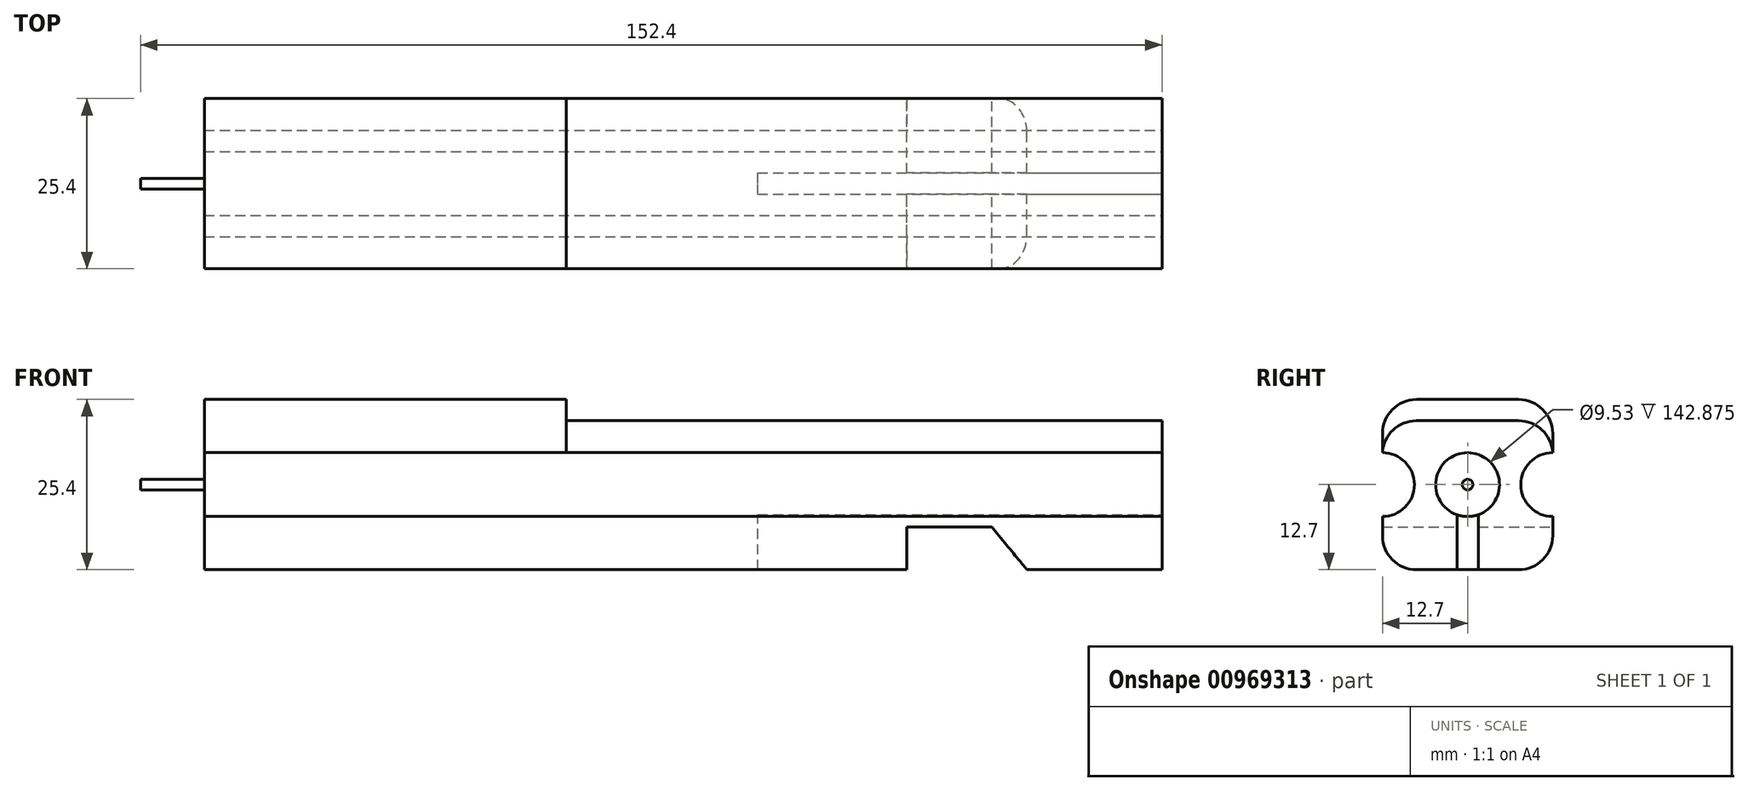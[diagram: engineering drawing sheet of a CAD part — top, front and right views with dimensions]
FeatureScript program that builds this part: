
annotation { "Feature Type Name" : "Feature", "Feature Type Description" : "" }
export const myFeature = defineFeature(function(context is Context, id is Id, definition is map)
    precondition{}
    {
        {
            var Q0;
            Q0=qCreatedBy(makeId("Front.planeOp"),FACE);
            var sketch = newSketch(context, id + "F0", { "sketchPlane" : qUnion([Q0])});
            skLineSegment(sketch, "E0.right", {"start": v(-83.92, 25.4) * mm, "end": v(-83.92, 0) * mm});
            skLineSegment(sketch, "E1.bottom", {"start": v(68.48, 7.94) * mm, "end": v(-74.4, 7.94) * mm});
            skLineSegment(sketch, "E1.top", {"start": v(68.48, 17.46) * mm, "end": v(-74.4, 17.46) * mm});
            skLineSegment(sketch, "E1.left", {"start": v(68.48, 7.94) * mm, "end": v(68.48, 17.46) * mm});
            skLineSegment(sketch, "E1.right", {"start": v(-74.4, 7.94) * mm, "end": v(-74.4, 17.46) * mm});
            skLineSegment(sketch, "E2", {"start": v(30.38, 0) * mm, "end": v(30.38, 6.35) * mm});
            skLineSegment(sketch, "E3", {"start": v(30.38, 6.35) * mm, "end": v(43.08, 6.35) * mm});
            skLineSegment(sketch, "E4", {"start": v(43.08, 6.35) * mm, "end": v(48.33, 0) * mm});
            skLineSegment(sketch, "E5", {"start": v(48.33, 0) * mm, "end": v(68.48, 0) * mm});
            skLineSegment(sketch, "E6", {"start": v(30.38, 0) * mm, "end": v(-83.92, 0) * mm});
            skLineSegment(sketch, "E7.top", {"start": v(68.48, 22.23) * mm, "end": v(-20.42, 22.23) * mm});
            skLineSegment(sketch, "E7.right", {"start": v(-20.42, 25.4) * mm, "end": v(-20.42, 22.23) * mm});
            skLineSegment(sketch, "E8", {"start": v(68.48, 22.23) * mm, "end": v(68.48, 0) * mm});
            skLineSegment(sketch, "E9", {"start": v(-20.42, 25.4) * mm, "end": v(-83.92, 25.4) * mm});
            skSolve(sketch);
        }
        {
            var Q0;
            Q0 = qSketchRegion(id + "F0", true);
            extrude(context, id + "F1", {"entities" : qUnion([Q0]), "endBound" : BoundingType.SYMMETRIC, "depth" : 25.4 * mm, "offsetDistance" : 25.4 * mm});
        }
        {
            var Q0;
            Q0=makeQuery(id+"F1.opExtrude","SWEPT_FACE",FACE,{"disambiguationData":[OSD([sQuery(id+"F0.wireOp",EDGE,"E8")])]});
            var sketch = newSketch(context, id + "F2", { "sketchPlane" : qUnion([Q0])});
            skLineSegment(sketch, "E10", {"start": v(0, 0) * mm, "end": v(0, 12.7) * mm});
            skCircle(sketch, "E11", {"center": v(0, 12.7) * mm, "radius": 4.76 * mm});
            skLineSegment(sketch, "E12", {"start": v(0, 12.7) * mm, "end": v(12.7, 12.7) * mm});
            skLineSegment(sketch, "E13", {"start": v(0, 12.7) * mm, "end": v(-12.7, 12.7) * mm});
            skCircle(sketch, "E14", {"center": v(12.7, 12.7) * mm, "radius": 4.76 * mm});
            skCircle(sketch, "E15", {"center": v(-12.7, 12.7) * mm, "radius": 4.76 * mm});
            skLineSegment(sketch, "E16.bottom", {"start": v(1.59, 0) * mm, "end": v(-1.59, 0) * mm});
            skLineSegment(sketch, "E16.top", {"start": v(1.59, 8.2) * mm, "end": v(-1.59, 8.2) * mm});
            skLineSegment(sketch, "E16.left", {"start": v(1.59, 0) * mm, "end": v(1.59, 8.2) * mm});
            skLineSegment(sketch, "E16.right", {"start": v(-1.59, 0) * mm, "end": v(-1.59, 8.2) * mm});
            skSolve(sketch);
        }
        {
            var Q0;
            Q0=makeQuery(id+"F2.imprint","IMPRINT",FACE,{"disambiguationData":[TD([[makeQuery(id+"F2.imprint","IMPRINT",EDGE,{"derivedFrom":sQuery(id+"F2.wireOp",EDGE,"E11")}),1.0]])]});
            var Q1;
            {var subQ1=sQuery(id+"F2.wireOp",EDGE,"E10");var subQ3=sQuery(id+"F2.wireOp",EDGE,"E16.top");var subQ4=makeQuery(id+"F2.imprint","INTERSECT",VERTEX,{"derivedFrom":[subQ1,subQ3]});Q1=makeQuery(id+"F2.imprint","IMPRINT",FACE,{"disambiguationData":[TD([[makeQuery(id+"F2.imprint","IMPRINT",EDGE,{"disambiguationData":[TD([[subQ4,-1.0]])],"derivedFrom":subQ1}),1.0]])]});}
            var Q2;
            {var subQ1=sQuery(id+"F2.wireOp",EDGE,"E10");var subQ3=sQuery(id+"F2.wireOp",EDGE,"E16.top");var subQ4=makeQuery(id+"F2.imprint","INTERSECT",VERTEX,{"derivedFrom":[subQ1,subQ3]});Q2=makeQuery(id+"F2.imprint","IMPRINT",FACE,{"disambiguationData":[TD([[makeQuery(id+"F2.imprint","IMPRINT",EDGE,{"disambiguationData":[TD([[subQ4,-1.0]])],"derivedFrom":subQ1}),-1.0]])]});}
            extrude(context, id + "F3", {"entities" : qUnion([Q0, Q1, Q2]), "operationType" : NewBodyOperationType.REMOVE, "oppositeDirection" : true, "depth" : 142.88 * mm, "offsetDistance" : 25.4 * mm});
        }
        {
            var Q0;
            Q0=makeQuery(id+"F1.opExtrude","SWEPT_FACE",FACE,{"disambiguationData":[OSD([sQuery(id+"F0.wireOp",EDGE,"E0.right")])]});
            var sketch = newSketch(context, id + "F4", { "sketchPlane" : qUnion([Q0])});
            skLineSegment(sketch, "E17", {"start": v(-12.7, 12.7) * mm, "end": v(12.7, 12.7) * mm});
            skCircle(sketch, "E18", {"center": v(0, 12.7) * mm, "radius": 0.8 * mm});
            skSolve(sketch);
        }
        {
            var Q0;
            {var subQ0=sQuery(id+"F4.wireOp",EDGE,"E18");var subQ1=sQuery(id+"F4.wireOp",EDGE,"E17");var subQ2=makeQuery(id+"F4.imprint","INTERSECT",VERTEX,{"disambiguationData":[OD(0.0)],"derivedFrom":[subQ1,subQ0]});Q0=makeQuery(id+"F4.imprint","IMPRINT",FACE,{"disambiguationData":[TD([[makeQuery(id+"F4.imprint","IMPRINT",EDGE,{"disambiguationData":[TD([[subQ2,-1.0]])],"derivedFrom":subQ1}),1.0]])]});}
            var Q1;
            {var subQ0=sQuery(id+"F4.wireOp",EDGE,"E18");var subQ1=sQuery(id+"F4.wireOp",EDGE,"E17");var subQ2=makeQuery(id+"F4.imprint","INTERSECT",VERTEX,{"disambiguationData":[OD(0.0)],"derivedFrom":[subQ1,subQ0]});Q1=makeQuery(id+"F4.imprint","IMPRINT",FACE,{"disambiguationData":[TD([[makeQuery(id+"F4.imprint","IMPRINT",EDGE,{"disambiguationData":[TD([[subQ2,-1.0]])],"derivedFrom":subQ1}),-1.0]])]});}
            extrude(context, id + "F5", {"entities" : qUnion([Q0, Q1]), "operationType" : NewBodyOperationType.REMOVE, "oppositeDirection" : true, "depth" : 9.52 * mm, "offsetDistance" : 25.4 * mm});
        }
        {
            var Q0;
            {var subQ0=sQuery(id+"F2.wireOp",EDGE,"E12");var subQ1=makeQuery(id+"F1.opExtrude","CAP_EDGE",EDGE,{"disambiguationData":[OSD([sQuery(id+"F0.wireOp",EDGE,"E8")])],"isStart":true});var subQ2=makeQuery(id+"F2.imprint","INTERSECT",VERTEX,{"derivedFrom":[subQ1,subQ0]});Q0=makeQuery(id+"F2.imprint","IMPRINT",FACE,{"disambiguationData":[TD([[makeQuery(id+"F2.imprint","IMPRINT",EDGE,{"disambiguationData":[TD([[subQ2,1.0]])],"derivedFrom":subQ0}),1.0]])]});}
            var Q1;
            {var subQ0=sQuery(id+"F2.wireOp",EDGE,"E12");var subQ1=makeQuery(id+"F1.opExtrude","CAP_EDGE",EDGE,{"disambiguationData":[OSD([sQuery(id+"F0.wireOp",EDGE,"E8")])],"isStart":true});var subQ2=makeQuery(id+"F2.imprint","INTERSECT",VERTEX,{"derivedFrom":[subQ1,subQ0]});Q1=makeQuery(id+"F2.imprint","IMPRINT",FACE,{"disambiguationData":[TD([[makeQuery(id+"F2.imprint","IMPRINT",EDGE,{"disambiguationData":[TD([[subQ2,1.0]])],"derivedFrom":subQ0}),-1.0]])]});}
            var Q2;
            {var subQ0=sQuery(id+"F2.wireOp",EDGE,"E13");var subQ1=makeQuery(id+"F1.opExtrude","CAP_EDGE",EDGE,{"disambiguationData":[OSD([sQuery(id+"F0.wireOp",EDGE,"E8")])],"isStart":false});var subQ2=makeQuery(id+"F2.imprint","INTERSECT",VERTEX,{"derivedFrom":[subQ1,subQ0]});Q2=makeQuery(id+"F2.imprint","IMPRINT",FACE,{"disambiguationData":[TD([[makeQuery(id+"F2.imprint","IMPRINT",EDGE,{"disambiguationData":[TD([[subQ2,1.0]])],"derivedFrom":subQ0}),1.0]])]});}
            var Q3;
            {var subQ0=sQuery(id+"F2.wireOp",EDGE,"E13");var subQ1=makeQuery(id+"F1.opExtrude","CAP_EDGE",EDGE,{"disambiguationData":[OSD([sQuery(id+"F0.wireOp",EDGE,"E8")])],"isStart":false});var subQ2=makeQuery(id+"F2.imprint","INTERSECT",VERTEX,{"derivedFrom":[subQ1,subQ0]});Q3=makeQuery(id+"F2.imprint","IMPRINT",FACE,{"disambiguationData":[TD([[makeQuery(id+"F2.imprint","IMPRINT",EDGE,{"disambiguationData":[TD([[subQ2,1.0]])],"derivedFrom":subQ0}),-1.0]])]});}
            extrude(context, id + "F6", {"entities" : qUnion([Q0, Q1, Q2, Q3]), "operationType" : NewBodyOperationType.REMOVE, "oppositeDirection" : true, "depth" : 142.88 * mm, "offsetDistance" : 25.4 * mm});
        }
        {
            var Q0;
            Q0=makeQuery(id+"F1.opExtrude","CAP_EDGE",EDGE,{"disambiguationData":[OSD([sQuery(id+"F0.wireOp",EDGE,"E7.top")])],"isStart":true});
            var Q1;
            Q1=makeQuery(id+"F1.opExtrude","CAP_EDGE",EDGE,{"disambiguationData":[OSD([sQuery(id+"F0.wireOp",EDGE,"E7.top")])],"isStart":false});
            var Q2;
            Q2=makeQuery(id+"F1.opExtrude","CAP_EDGE",EDGE,{"disambiguationData":[OSD([sQuery(id+"F0.wireOp",EDGE,"E5")])],"isStart":true});
            var Q3;
            Q3=makeQuery(id+"F1.opExtrude","CAP_EDGE",EDGE,{"disambiguationData":[OSD([sQuery(id+"F0.wireOp",EDGE,"E5")])],"isStart":false});
            var Q4;
            Q4=makeQuery(id+"F1.opExtrude","CAP_EDGE",EDGE,{"disambiguationData":[OSD([sQuery(id+"F0.wireOp",EDGE,"E6")])],"isStart":false});
            var Q5;
            Q5=makeQuery(id+"F1.opExtrude","CAP_EDGE",EDGE,{"disambiguationData":[OSD([sQuery(id+"F0.wireOp",EDGE,"E6")])],"isStart":true});
            fillet(context, id + "F7", {"entities" : qUnion([Q0, Q1, Q2, Q3, Q4, Q5]), "radius" : 5.08 * mm, "tangentPropagation" : true, "allowEdgeOverflow" : false});
        }
        {
            var Q0;
            Q0=makeQuery(id+"F1.opExtrude","CAP_EDGE",EDGE,{"disambiguationData":[OSD([sQuery(id+"F0.wireOp",EDGE,"E9")])],"isStart":true});
            var Q1;
            Q1=makeQuery(id+"F1.opExtrude","CAP_EDGE",EDGE,{"disambiguationData":[OSD([sQuery(id+"F0.wireOp",EDGE,"E9")])],"isStart":false});
            fillet(context, id + "F8", {"entities" : qUnion([Q0, Q1]), "radius" : 5.08 * mm, "tangentPropagation" : true, "allowEdgeOverflow" : false});
        }
        {
            var Q0;
            {var subQ5=sQuery(id+"F2.wireOp",EDGE,"E16.left");Q0=makeQuery(id+"F2.imprint","IMPRINT",FACE,{"disambiguationData":[TD([[makeQuery(id+"F2.imprint","IMPRINT",EDGE,{"derivedFrom":subQ5}),1.0]])]});}
            var Q1;
            {var subQ5=sQuery(id+"F2.wireOp",EDGE,"E16.right");Q1=makeQuery(id+"F2.imprint","IMPRINT",FACE,{"disambiguationData":[TD([[makeQuery(id+"F2.imprint","IMPRINT",EDGE,{"derivedFrom":subQ5}),-1.0]])]});}
            extrude(context, id + "F9", {"entities" : qUnion([Q0, Q1]), "operationType" : NewBodyOperationType.REMOVE, "oppositeDirection" : true, "depth" : 60.32 * mm, "offsetDistance" : 25.4 * mm});
        }
    });
